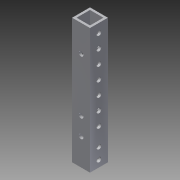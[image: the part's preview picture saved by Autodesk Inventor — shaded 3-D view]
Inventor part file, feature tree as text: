
AUTODESK INVENTOR PART (.ipt)
format: ipt  version: 2013 (Build 170138000, 138)  size: 144,896 bytes
history: native  units: in
note: dims shown in document units (in); Inventor stores cm internally (conversion verified against a paired STEP export)
features: extrude x4, sketch x4, reference x2
ambient origin geometry x8: Origin, YZ Plane, XZ Plane, XY Plane, X Axis, Y Axis, Z Axis, Center Point
bodies: Solid1 (feature_tree)
feature tree (10):
  extrude  "Extrusion1"  Depth=1.0in
  extrude  "Extrusion2"  Depth=7.0in TaperAngle=0.0deg
  extrude  "Extrusion3"  Depth=0.26in
  extrude  "Extrusion4"  Depth=4.25in
  sketch  "Sketch1"  dims[d0=1.0in d1=1.0in]
  sketch  "Sketch2"  dims[d2=0.125in d3=7.0in d4=0.0in]
  reference  "Reference1"
  reference  "Reference2"
  sketch  "Sketch3"  dims[d7=1.0in d8=0.0in d17=0.26in]
  sketch  "Sketch4"  dims[d18=0.26in d19=4.25in d20=0.26in d21=0.5in d22=0.5in d23=0.26in d25=1.0in d26=2.3622in d28=0.75in d29=0.3937in d31=1.0in d33=1.0in d34=0.0in d35=1.5in d36=0.26in d37=1.9685in d39=1.0in d40=0.3937in d42=1.0in d44=1.0in d45=0.0in]
